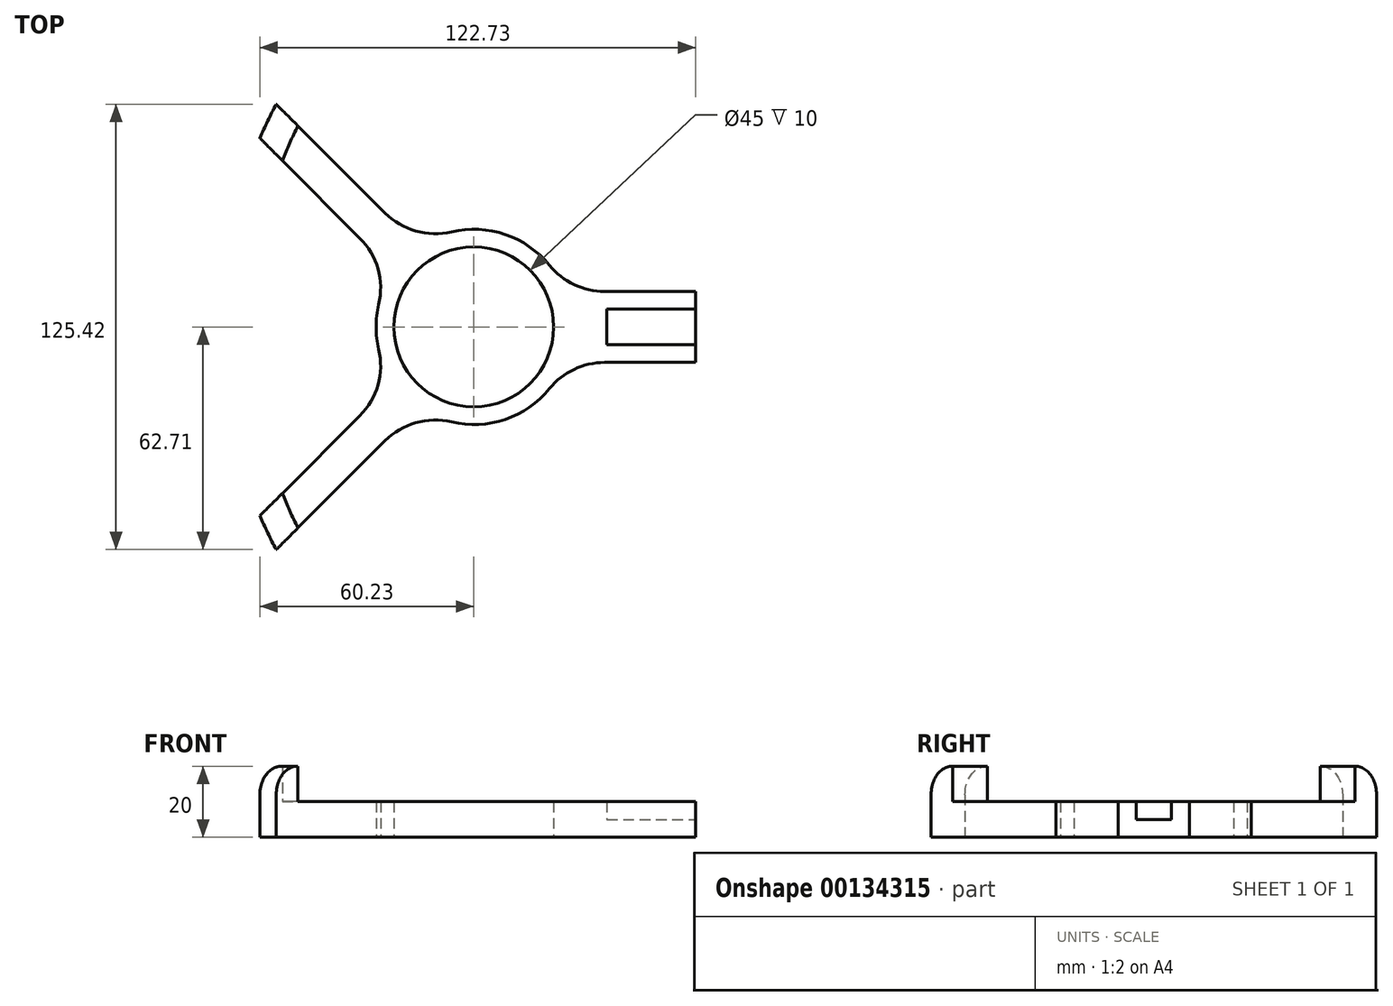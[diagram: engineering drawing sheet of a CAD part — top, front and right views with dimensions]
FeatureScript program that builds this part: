
annotation { "Feature Type Name" : "Feature", "Feature Type Description" : "" }
export const myFeature = defineFeature(function(context is Context, id is Id, definition is map)
    precondition{}
    {
        {
            var Q0;
            Q0=qCreatedBy(makeId("Top.planeOp"),FACE);
            var sketch = newSketch(context, id + "F0", { "sketchPlane" : qUnion([Q0])});
            skCircle(sketch, "E0", {"center": v(-62.5, 0) * mm, "radius": 22.5 * mm});
            skCircle(sketch, "E1", {"center": v(-62.5, 0) * mm, "radius": 27.5 * mm});
            skCircle(sketch, "E2.MirrorC", {"center": v(62.5, 0) * mm, "radius": 22.5 * mm});
            skCircle(sketch, "E3.MirrorC", {"center": v(62.5, 0) * mm, "radius": 27.5 * mm});
            skLineSegment(sketch, "E4", {"start": v(-125, 0) * mm, "end": v(-125, 16.16) * mm});
            skLineSegment(sketch, "E5.bottom", {"start": v(-36.88, 10) * mm, "end": v(36.88, 10) * mm});
            skLineSegment(sketch, "E5.top", {"start": v(-36.88, -10) * mm, "end": v(36.88, -10) * mm});
            skLineSegment(sketch, "E6.bottom", {"start": v(-125.1, 10) * mm, "end": v(-125, 10) * mm});
            skLineSegment(sketch, "E6.top", {"start": v(-125.1, -10) * mm, "end": v(-125, -10) * mm});
            skLineSegment(sketch, "E6.left", {"start": v(-125, 10) * mm, "end": v(-125, -10) * mm});
            skLineSegment(sketch, "E7.top", {"start": v(87.83, -4.12) * mm, "end": v(89.69, -4.12) * mm});
            skCircle(sketch, "E8", {"center": v(0, 0) * mm, "radius": 125.5 * mm});
            skLineSegment(sketch, "E9", {"start": v(-62.5, 0) * mm, "end": v(-62.5, 10.08) * mm});
            skLineSegment(sketch, "E10", {"start": v(-62.5, 0) * mm, "end": v(-114.3, -51.8) * mm});
            skLineSegment(sketch, "E11", {"start": v(-62.5, 0) * mm, "end": v(-114.3, 51.8) * mm});
            skLineSegment(sketch, "E12", {"start": v(-78.09, 22.66) * mm, "end": v(-118.14, 62.7) * mm});
            skLineSegment(sketch, "E13", {"start": v(-85.16, 15.59) * mm, "end": v(-122.73, 53.16) * mm});
            skCircle(sketch, "E14", {"center": v(0, 0) * mm, "radius": 133.75 * mm});
            skLineSegment(sketch, "E15.MirrorCS", {"start": v(-85.16, -15.59) * mm, "end": v(-122.73, -53.16) * mm});
            skLineSegment(sketch, "E16.MirrorCS", {"start": v(-78.09, -22.66) * mm, "end": v(-118.14, -62.7) * mm});
            skLineSegment(sketch, "E17.MirrorCS", {"start": v(85.16, -15.59) * mm, "end": v(122.73, -53.16) * mm});
            skLineSegment(sketch, "E18.MirrorCS", {"start": v(78.09, -22.66) * mm, "end": v(118.14, -62.7) * mm});
            skLineSegment(sketch, "E19.MirrorCS", {"start": v(85.16, 15.59) * mm, "end": v(122.73, 53.16) * mm});
            skLineSegment(sketch, "E20.MirrorCS", {"start": v(78.09, 22.66) * mm, "end": v(118.14, 62.7) * mm});
            skPoint(sketch, "E21.MirrorCS.end.orphan", {"position": v(125, 16.16) * mm});
            skPoint(sketch, "E21.MirrorCS.start.orphan", {"position": v(125, 0) * mm});
            skLineSegment(sketch, "E22", {"start": v(0, 10) * mm, "end": v(0, -10) * mm});
            skLineSegment(sketch, "E23.bottom", {"start": v(-25, 5) * mm, "end": v(25, 5) * mm});
            skLineSegment(sketch, "E23.top", {"start": v(-25, -5) * mm, "end": v(25, -5) * mm});
            skLineSegment(sketch, "E23.left", {"start": v(-25, 5) * mm, "end": v(-25, -5) * mm});
            skLineSegment(sketch, "E23.right", {"start": v(25, 5) * mm, "end": v(25, -5) * mm});
            skSolve(sketch);
        }
        {
            var Q0;
            {var subQ5=sQuery(id+"F0.wireOp",EDGE,"E22");Q0=makeQuery(id+"F0.imprint","IMPRINT",FACE,{"disambiguationData":[TD([[makeQuery(id+"F0.imprint","IMPRINT",EDGE,{"derivedFrom":subQ5}),-1.0]])]});}
            var Q1;
            {var subQ0=sQuery(id+"F0.wireOp",EDGE,"E12");var subQ1=sQuery(id+"F0.wireOp",EDGE,"E1");var subQ2=makeQuery(id+"F0.imprint","INTERSECT",VERTEX,{"derivedFrom":[subQ1,subQ0]});Q1=makeQuery(id+"F0.imprint","IMPRINT",FACE,{"disambiguationData":[TD([[makeQuery(id+"F0.imprint","IMPRINT",EDGE,{"disambiguationData":[TD([[subQ2,-1.0]])],"derivedFrom":subQ1}),-1.0]])]});}
            var Q2;
            {var subQ0=sQuery(id+"F0.wireOp",EDGE,"E13");var subQ1=sQuery(id+"F0.wireOp",EDGE,"E1");var subQ2=makeQuery(id+"F0.imprint","INTERSECT",VERTEX,{"derivedFrom":[subQ1,subQ0]});Q2=makeQuery(id+"F0.imprint","IMPRINT",FACE,{"disambiguationData":[TD([[makeQuery(id+"F0.imprint","IMPRINT",EDGE,{"disambiguationData":[TD([[subQ2,1.0]])],"derivedFrom":subQ1}),-1.0]])]});}
            var Q3;
            {var subQ2=sQuery(id+"F0.wireOp",EDGE,"E10");var subQ9=sQuery(id+"F0.wireOp",EDGE,"E0");var subQ10=makeQuery(id+"F0.imprint","INTERSECT",VERTEX,{"derivedFrom":[subQ9,subQ2]});Q3=makeQuery(id+"F0.imprint","IMPRINT",FACE,{"disambiguationData":[TD([[makeQuery(id+"F0.imprint","IMPRINT",EDGE,{"disambiguationData":[TD([[subQ10,-1.0]])],"derivedFrom":subQ9}),-1.0]])]});}
            var Q4;
            {var subQ2=sQuery(id+"F0.wireOp",EDGE,"E10");var subQ6=sQuery(id+"F0.wireOp",EDGE,"E0");var subQ9=makeQuery(id+"F0.imprint","INTERSECT",VERTEX,{"derivedFrom":[subQ6,subQ2]});Q4=makeQuery(id+"F0.imprint","IMPRINT",FACE,{"disambiguationData":[TD([[makeQuery(id+"F0.imprint","IMPRINT",EDGE,{"disambiguationData":[TD([[subQ9,1.0]])],"derivedFrom":subQ6}),-1.0]])]});}
            var Q5;
            {var subQ0=sQuery(id+"F0.wireOp",EDGE,"E15.MirrorCS");var subQ1=sQuery(id+"F0.wireOp",EDGE,"E1");var subQ2=makeQuery(id+"F0.imprint","INTERSECT",VERTEX,{"derivedFrom":[subQ1,subQ0]});Q5=makeQuery(id+"F0.imprint","IMPRINT",FACE,{"disambiguationData":[TD([[makeQuery(id+"F0.imprint","IMPRINT",EDGE,{"disambiguationData":[TD([[subQ2,-1.0]])],"derivedFrom":subQ1}),-1.0]])]});}
            var Q6;
            {var subQ0=sQuery(id+"F0.wireOp",EDGE,"E16.MirrorCS");var subQ1=sQuery(id+"F0.wireOp",EDGE,"E1");var subQ2=makeQuery(id+"F0.imprint","INTERSECT",VERTEX,{"derivedFrom":[subQ1,subQ0]});Q6=makeQuery(id+"F0.imprint","IMPRINT",FACE,{"disambiguationData":[TD([[makeQuery(id+"F0.imprint","IMPRINT",EDGE,{"disambiguationData":[TD([[subQ2,1.0]])],"derivedFrom":subQ1}),-1.0]])]});}
            var Q7;
            {var subQ3=sQuery(id+"F0.wireOp",EDGE,"E8");var subQ7=makeQuery(id+"F0.imprint","INTERSECT",VERTEX,{"derivedFrom":[subQ3,sQuery(id+"F0.wireOp",EDGE,"E10")]});Q7=makeQuery(id+"F0.imprint","IMPRINT",FACE,{"disambiguationData":[TD([[makeQuery(id+"F0.imprint","IMPRINT",EDGE,{"disambiguationData":[TD([[subQ7,1.0]])],"derivedFrom":subQ3}),-1.0]])]});}
            var Q8;
            {var subQ3=sQuery(id+"F0.wireOp",EDGE,"E8");var subQ8=makeQuery(id+"F0.imprint","INTERSECT",VERTEX,{"derivedFrom":[subQ3,sQuery(id+"F0.wireOp",EDGE,"E11")]});Q8=makeQuery(id+"F0.imprint","IMPRINT",FACE,{"disambiguationData":[TD([[makeQuery(id+"F0.imprint","IMPRINT",EDGE,{"disambiguationData":[TD([[subQ8,1.0]])],"derivedFrom":subQ3}),-1.0]])]});}
            extrude(context, id + "F1", {"entities" : qUnion([Q0, Q1, Q2, Q3, Q4, Q5, Q6, Q7, Q8]), "depth" : 10 * mm});
        }
        {
            var Q0;
            Q0=makeQuery(id+"F1.opExtrude","SWEPT_EDGE",EDGE,{"disambiguationData":[OSD([sQuery(id+"F0.wireOp",EDGE,"E1"),sQuery(id+"F0.wireOp",EDGE,"E16.MirrorCS")])]});
            var Q1;
            Q1=makeQuery(id+"F1.opExtrude","SWEPT_EDGE",EDGE,{"disambiguationData":[OSD([sQuery(id+"F0.wireOp",EDGE,"E1"),sQuery(id+"F0.wireOp",EDGE,"E5.top")])]});
            var Q2;
            Q2=makeQuery(id+"F1.opExtrude","SWEPT_EDGE",EDGE,{"disambiguationData":[OSD([sQuery(id+"F0.wireOp",EDGE,"E1"),sQuery(id+"F0.wireOp",EDGE,"E5.bottom")])]});
            var Q3;
            Q3=makeQuery(id+"F1.opExtrude","SWEPT_EDGE",EDGE,{"disambiguationData":[OSD([sQuery(id+"F0.wireOp",EDGE,"E1"),sQuery(id+"F0.wireOp",EDGE,"E12")])]});
            var Q4;
            Q4=makeQuery(id+"F1.opExtrude","SWEPT_EDGE",EDGE,{"disambiguationData":[OSD([sQuery(id+"F0.wireOp",EDGE,"E1"),sQuery(id+"F0.wireOp",EDGE,"E15.MirrorCS")])]});
            var Q5;
            Q5=makeQuery(id+"F1.opExtrude","SWEPT_EDGE",EDGE,{"disambiguationData":[OSD([sQuery(id+"F0.wireOp",EDGE,"E1"),sQuery(id+"F0.wireOp",EDGE,"E13")])]});
            fillet(context, id + "F2", {"entities" : qUnion([Q0, Q1, Q2, Q3, Q4, Q5]), "radius" : 20 * mm, "tangentPropagation" : true, "allowEdgeOverflow" : false});
        }
        {
            var Q0;
            {var subQ3=sQuery(id+"F0.wireOp",EDGE,"E8");var subQ8=makeQuery(id+"F0.imprint","INTERSECT",VERTEX,{"derivedFrom":[subQ3,sQuery(id+"F0.wireOp",EDGE,"E11")]});Q0=makeQuery(id+"F0.imprint","IMPRINT",FACE,{"disambiguationData":[TD([[makeQuery(id+"F0.imprint","IMPRINT",EDGE,{"disambiguationData":[TD([[subQ8,1.0]])],"derivedFrom":subQ3}),-1.0]])]});}
            var Q1;
            {var subQ3=sQuery(id+"F0.wireOp",EDGE,"E8");var subQ7=makeQuery(id+"F0.imprint","INTERSECT",VERTEX,{"derivedFrom":[subQ3,sQuery(id+"F0.wireOp",EDGE,"E10")]});Q1=makeQuery(id+"F0.imprint","IMPRINT",FACE,{"disambiguationData":[TD([[makeQuery(id+"F0.imprint","IMPRINT",EDGE,{"disambiguationData":[TD([[subQ7,1.0]])],"derivedFrom":subQ3}),-1.0]])]});}
            extrude(context, id + "F3", {"entities" : qUnion([Q0, Q1]), "operationType" : NewBodyOperationType.ADD, "depth" : 20 * mm});
        }
        {
            var Q0;
            {var subQ5=sQuery(id+"F0.wireOp",EDGE,"E23.left");Q0=makeQuery(id+"F0.imprint","IMPRINT",FACE,{"disambiguationData":[TD([[makeQuery(id+"F0.imprint","IMPRINT",EDGE,{"derivedFrom":subQ5}),1.0]])]});}
            extrude(context, id + "F4", {"entities" : qUnion([Q0]), "operationType" : NewBodyOperationType.ADD, "depth" : 5 * mm});
        }
        {
            var Q0;
            {var subQ0=sQuery(id+"F0.wireOp",EDGE,"E14");Q0=makeQuery(id+"F3.opExtrude","CAP_EDGE",EDGE,{"disambiguationData":[OSD([subQ0]),TDD([makeQuery(id+"F0.imprint","IMPRINT",EDGE,{"disambiguationData":[TD([[makeQuery(id+"F0.imprint","INTERSECT",VERTEX,{"derivedFrom":[subQ0,sQuery(id+"F0.wireOp",EDGE,"E15.MirrorCS")]}),-1.0]])],"derivedFrom":subQ0})])],"isStart":false});}
            var Q1;
            {var subQ0=sQuery(id+"F0.wireOp",EDGE,"E14");Q1=makeQuery(id+"F3.opExtrude","CAP_EDGE",EDGE,{"disambiguationData":[OSD([subQ0]),TDD([makeQuery(id+"F0.imprint","IMPRINT",EDGE,{"disambiguationData":[TD([[makeQuery(id+"F0.imprint","INTERSECT",VERTEX,{"derivedFrom":[sQuery(id+"F0.wireOp",EDGE,"E12"),subQ0]}),-1.0]])],"derivedFrom":subQ0})])],"isStart":false});}
            fillet(context, id + "F5", {"entities" : qUnion([Q0, Q1]), "radius" : 8 * mm, "tangentPropagation" : true, "allowEdgeOverflow" : false});
        }
    });
